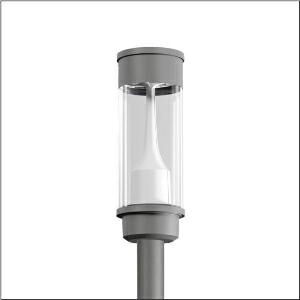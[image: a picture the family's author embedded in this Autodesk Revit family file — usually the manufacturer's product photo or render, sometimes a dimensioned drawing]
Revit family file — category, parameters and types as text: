
# Revit family: litepole_iq___st1_2a_5xa5415af14h_245c
name_source: partatom
category: Lighting Fixtures
units: mm (PartAtom-declared; Revit-internal decimal feet)

## family parameters
Cut with Voids When Loaded = No
Host = Face
Light Source = No
Part Type = Normal
Room Calculation Point = No
Round Connector Dimension = Use Diameter
Shared = No

## types (1)
- --- (1 x LED, 1540 lm, 12.9 W, 2200K)
    Apparent Load = 13 VA
    CIE Flux Codes = 22 61 93 96 100
    Color Rendering = 70
    Color Temperature = 2200K
    Default Elevation = 1800 mm
    Description = Litepole iQ, mast luminaire, Module 540 iQ-SR, primary light control with 3 zone facetted reflector, of plastic, silver coated, highly specular, structured, primary optical cover: cover, of PMMA, transparent, partly coated, light distribution: ST1.2a, light emission: direct distribution, primary light characteristic: asymmetric, installation type: post-top, LED, High Power LED, rated luminous flux: 1.540lm, luminous efficacy: 119lm/W, light colour: 722, colour temperature: 2200K, control gear: ECG iQ, control: optimised constant luminous flux control (CLO 2.0), Desk-Remote (wireless, voltage-free reading and setting of iQ features in the workshop via application-optimized NFC function/RFID function), Light-Fading, Smart-Wire, Night-Set, Lumen-Switch, Temp-Guard, Auto-Match, Street-Remote, presetting dimming logarithmic, with terminal, 6-pole, max. 2.5mm², mains connection: 230..240V, AC, 50/60Hz, start of lifetime: 13W, end of service life: 13W, reduction: 6W, luminaire housing, upper part, of glass-fibre reinforced polyester, coated, Siteco® metallic grey (DB 702S), diameter: 210mm, height: 590mm, spigot size: d x l = 76 x 70mm (post-top) | with reducer (optional accessory) 60 x 70mm, post-top mast mounting element, of diecast aluminium, coated, Siteco® metallic grey (DB 702S), Module 540 iQ-SR, traffic white (RAL 9016), equipment: standard, protection rating (complete): IP65, insulation class (complete): insulation class II (safety insulation), certification: CE, ENEC, VDE, packaging unit: 1 piece

Light Distribution: ST1.2a
    Height = 590 mm
    Lamp = 1 x LED
    Lamp Light Flux = 1540 lm
    Lamp Power = 12.9 W
    Lamp count = 1
    Length = 220 mm
    Luminous efficacy = 119 lm/W
    Manufacturer = Siteco
    ModVariant = No
    Model = 5XA5415AF14H
    Number of Poles = 1
    OnlyDefault = Yes
    Power Factor = 1
    Product Name = Litepole iQ | ST1.2a
    Product group = mast luminaire | pylon top
    ProductGroupID = 6100
    Protection Class = Protection class II
    Protection Degree = IP 65
    RLX_Detail_Level = 1
    RLX_Emergency_Light_Flux = 0 lm
    RLX_Emergency_Type = 0
    RLX_Emergency_Type_DB = No
    RlxData = <blob elided: 72741 chars, md5=ea80a1d9>
    Socket = socket
    Standby Power = 0 W
    System Light Flux = 1540 lm
    System Power = 13 W
    Type Comments = factory setting: luminous flux: 100 % | dim-lin: 254 | 516 mA
    Type Image = l_1006025.jpg
    URL = http://relux.com
    VarID = @adj_091215
    Voltage = 0 V
    Weight = 0.00 kg
    Width = 0 mm  [stored 0 ft]

note: [stored X ft] marks values corroborated as IEEE doubles in the binary element streams (Revit-internal decimal feet)

## geometry (parser evidence)
native form markers: Blend x4, Sweep x10
no freeform markers — native parametric forms only
